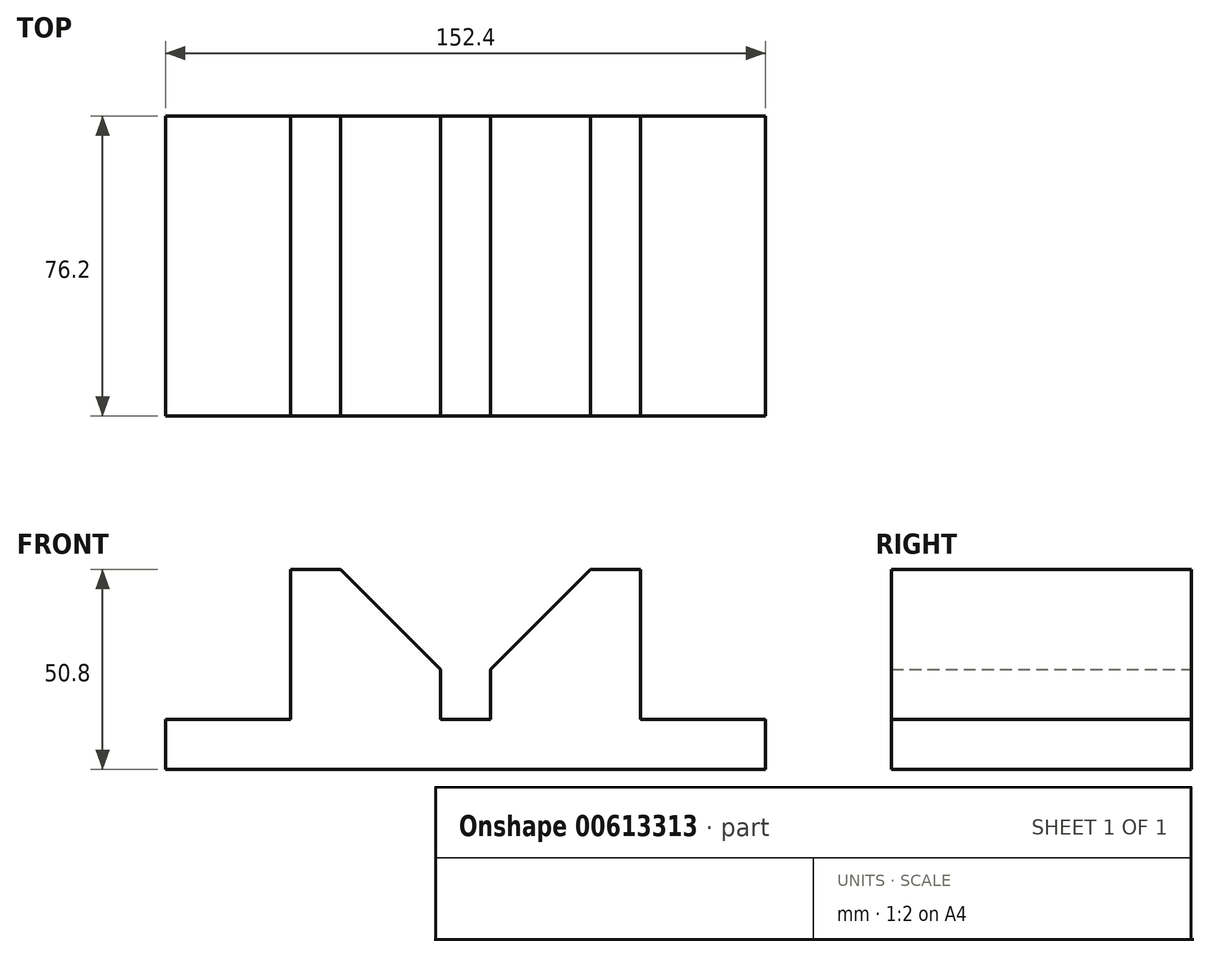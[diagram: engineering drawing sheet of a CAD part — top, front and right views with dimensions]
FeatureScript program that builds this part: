
annotation { "Feature Type Name" : "Feature", "Feature Type Description" : "" }
export const myFeature = defineFeature(function(context is Context, id is Id, definition is map)
    precondition{}
    {
        {
            var Q0;
            Q0=qCreatedBy(makeId("Front.planeOp"),FACE);
            var sketch = newSketch(context, id + "F0", { "sketchPlane" : qUnion([Q0])});
            skLineSegment(sketch, "E0", {"start": v(0, 0) * mm, "end": v(-31.75, 0) * mm});
            skLineSegment(sketch, "E1", {"start": v(-31.75, 0) * mm, "end": v(-31.75, -12.7) * mm});
            skLineSegment(sketch, "E2", {"start": v(-31.75, -12.7) * mm, "end": v(120.65, -12.7) * mm});
            skLineSegment(sketch, "E3", {"start": v(120.65, -12.7) * mm, "end": v(120.65, 0) * mm});
            skLineSegment(sketch, "E4", {"start": v(120.65, 0) * mm, "end": v(88.9, 0) * mm});
            skLineSegment(sketch, "E5", {"start": v(0, 0) * mm, "end": v(0, 38.1) * mm});
            skLineSegment(sketch, "E6", {"start": v(0, 38.1) * mm, "end": v(12.7, 38.1) * mm});
            skLineSegment(sketch, "E7", {"start": v(38.1, 0) * mm, "end": v(38.1, 12.7) * mm});
            skLineSegment(sketch, "E8", {"start": v(12.7, 38.1) * mm, "end": v(38.1, 12.7) * mm});
            skLineSegment(sketch, "E9", {"start": v(38.1, 0) * mm, "end": v(50.8, 0) * mm});
            skLineSegment(sketch, "E10", {"start": v(50.8, 0) * mm, "end": v(50.8, 12.7) * mm});
            skLineSegment(sketch, "E11", {"start": v(88.9, 0) * mm, "end": v(88.9, 38.1) * mm});
            skLineSegment(sketch, "E12", {"start": v(88.9, 38.1) * mm, "end": v(76.2, 38.1) * mm});
            skLineSegment(sketch, "E13", {"start": v(76.2, 38.1) * mm, "end": v(50.8, 12.7) * mm});
            skSolve(sketch);
        }
        {
            var Q0;
            Q0 = qSketchRegion(id + "F0", true);
            extrude(context, id + "F1", {"entities" : qUnion([Q0]), "depth" : 76.2 * mm, "offsetDistance" : 25.4 * mm});
        }
    });
